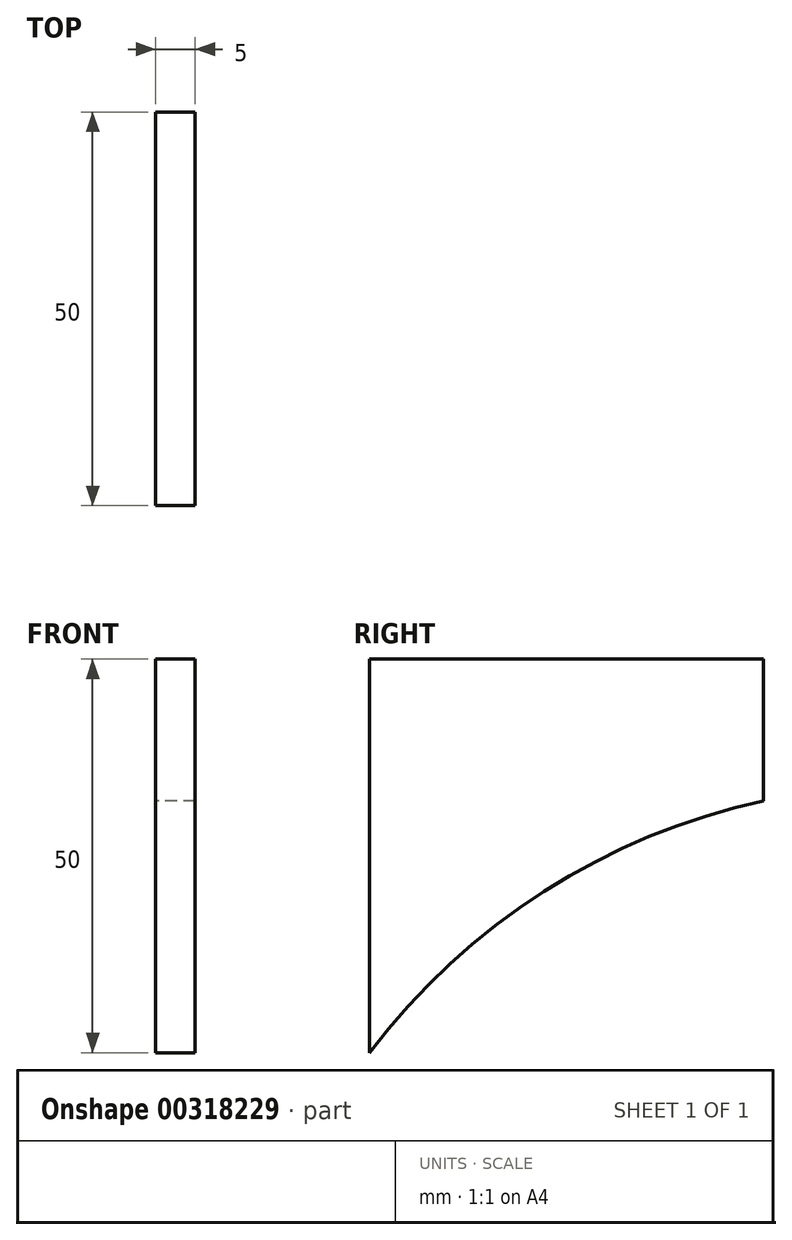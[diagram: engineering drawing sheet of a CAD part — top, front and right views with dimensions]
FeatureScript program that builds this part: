
annotation { "Feature Type Name" : "Feature", "Feature Type Description" : "" }
export const myFeature = defineFeature(function(context is Context, id is Id, definition is map)
    precondition{}
    {
        {
            var Q0;
            Q0=qCreatedBy(makeId("Front.planeOp"),FACE);
            var sketch = newSketch(context, id + "F0", { "sketchPlane" : qUnion([Q0])});
            skLineSegment(sketch, "E0.bottom", {"start": v(2.5, 25) * mm, "end": v(-2.5, 25) * mm});
            skLineSegment(sketch, "E0.top", {"start": v(2.5, -25) * mm, "end": v(-2.5, -25) * mm});
            skLineSegment(sketch, "E0.left", {"start": v(2.5, 25) * mm, "end": v(2.5, -25) * mm});
            skLineSegment(sketch, "E0.right", {"start": v(-2.5, 25) * mm, "end": v(-2.5, -25) * mm});
            skPoint(sketch, "E0.middle", {"position": v(0, 0) * mm});
            skSolve(sketch);
        }
        {
            var Q0;
            Q0=qCreatedBy(makeId("Front.planeOp"),FACE);
            cPlane(context, id + "F1", {"entities" : qUnion([Q0]), "cplaneType" : CPlaneType.OFFSET, "offset" : 50 * mm, "oppositeDirection" : true, "width" : 150 * mm, "height" : 150 * mm});
        }
        {
            var Q0;
            Q0=qCreatedBy(id+"F1.planeOp",FACE);
            var sketch = newSketch(context, id + "F2", { "sketchPlane" : qUnion([Q0])});
            skLineSegment(sketch, "E1.bottom", {"start": v(-2.5, 25) * mm, "end": v(2.5, 25) * mm});
            skLineSegment(sketch, "E1.top", {"start": v(-2.5, -5) * mm, "end": v(2.5, -5) * mm});
            skLineSegment(sketch, "E1.left", {"start": v(-2.5, 25) * mm, "end": v(-2.5, -5) * mm});
            skLineSegment(sketch, "E1.right", {"start": v(2.5, 25) * mm, "end": v(2.5, -5) * mm});
            skPoint(sketch, "E1.middle", {"position": v(0, 10) * mm});
            skSolve(sketch);
        }
        {
            var Q0;
            Q0 = qSketchRegion(id + "F0", true);
            var Q1;
            Q1 = qSketchRegion(id + "F2", true);
            loft(context, id + "F3", {"sheetProfilesArray" : [{ "sheetProfileEntities" : qUnion([Q0]) }, { "sheetProfileEntities" : qUnion([Q1]) }]});
        }
        {
            var Q0;
            Q0=makeQuery(id+"F3.opLoft","SWEPT_FACE",FACE,{"disambiguationData":[OSD([sQuery(id+"F0.wireOp",EDGE,"E0.bottom"),sQuery(id+"F0.wireOp",EDGE,"E0.top"),sQuery(id+"F0.wireOp",EDGE,"E0.right"),sQuery(id+"F2.wireOp",EDGE,"E1.bottom"),sQuery(id+"F2.wireOp",EDGE,"E1.top"),sQuery(id+"F2.wireOp",EDGE,"E1.left")])]});
            var sketch = newSketch(context, id + "F4", { "sketchPlane" : qUnion([Q0])});
            skArc(sketch, "E2", {"start": v(0, -25) * mm, "mid": v(-22.12, -4.52) * mm, "end": v(-50, 6.96) * mm});
            skLineSegment(sketch, "E3.0", {"start": v(-50, -5) * mm, "end": v(-50, 6.96) * mm});
            skLineSegment(sketch, "E4.0", {"start": v(0, -25) * mm, "end": v(-50, -5) * mm});
            skPoint(sketch, "E5.orphan", {"position": v(-50, 25) * mm});
            skSolve(sketch);
        }
        {
            var Q0;
            Q0 = qSketchRegion(id + "F4", true);
            extrude(context, id + "F5", {"entities" : qUnion([Q0]), "operationType" : NewBodyOperationType.REMOVE, "oppositeDirection" : true, "depth" : 25 * mm});
        }
    });
